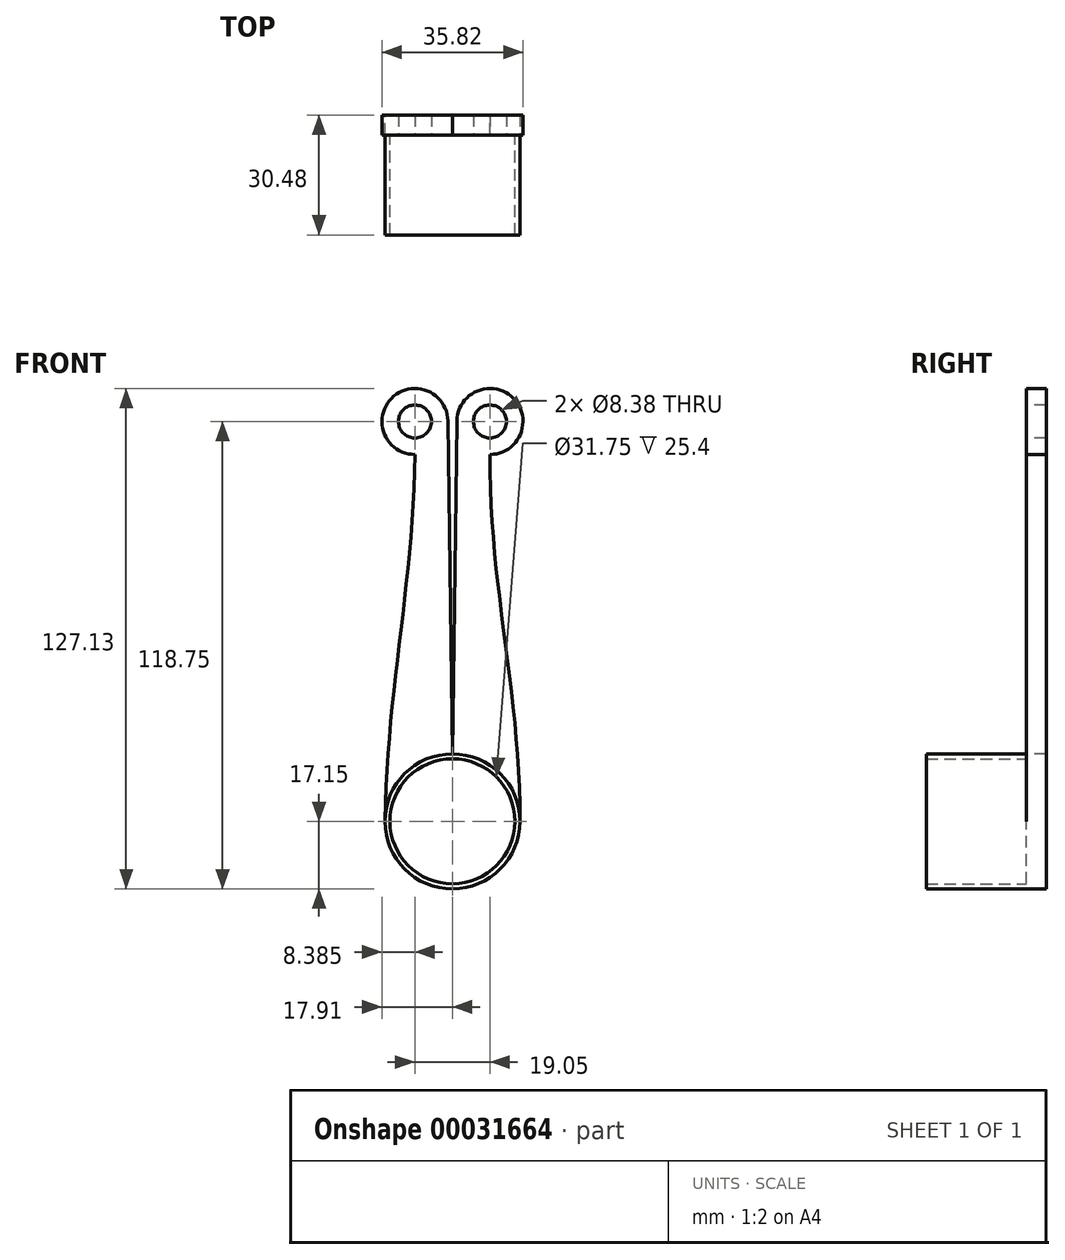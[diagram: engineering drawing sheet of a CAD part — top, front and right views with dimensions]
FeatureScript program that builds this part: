
annotation { "Feature Type Name" : "Feature", "Feature Type Description" : "" }
export const myFeature = defineFeature(function(context is Context, id is Id, definition is map)
    precondition{}
    {
        {
            var Q0;
            Q0=qCreatedBy(makeId("Front.planeOp"),FACE);
            var sketch = newSketch(context, id + "F0", { "sketchPlane" : qUnion([Q0])});
            skCircle(sketch, "E0", {"center": v(0, 0) * mm, "radius": 15.88 * mm});
            skCircle(sketch, "E1", {"center": v(0, 0) * mm, "radius": 17.15 * mm});
            skSolve(sketch);
        }
        {
            var Q0;
            Q0=makeQuery(id+"F0.imprint","IMPRINT",FACE,{"disambiguationData":[TD([[makeQuery(id+"F0.imprint","IMPRINT",EDGE,{"derivedFrom":sQuery(id+"F0.wireOp",EDGE,"E0")}),-1.0]])]});
            extrude(context, id + "F1", {"entities" : qUnion([Q0]), "depth" : 25.4 * mm});
        }
        {
            var Q0;
            Q0=makeQuery(id+"F1.opExtrude","CAP_FACE",FACE,{"disambiguationData":[OSD([sQuery(id+"F0.wireOp",EDGE,"E0"),sQuery(id+"F0.wireOp",EDGE,"E1")])],"isStart":true});
            var sketch = newSketch(context, id + "F2", { "sketchPlane" : qUnion([Q0])});
            skCircle(sketch, "E2", {"center": v(0, 0) * mm, "radius": 17.15 * mm});
            skSolve(sketch);
        }
        {
            var Q0;
            Q0 = qSketchRegion(id + "F2", true);
            extrude(context, id + "F3", {"entities" : qUnion([Q0]), "operationType" : NewBodyOperationType.ADD, "depth" : 5.08 * mm});
        }
        {
            var Q0;
            Q0=makeQuery(id+"F3.opExtrude","CAP_FACE",FACE,{"disambiguationData":[OSD([sQuery(id+"F2.wireOp",EDGE,"E2")])],"isStart":true});
            var sketch = newSketch(context, id + "F4", { "sketchPlane" : qUnion([Q0])});
            skCircle(sketch, "E3", {"center": v(9.52, 101.6) * mm, "radius": 4.2 * mm});
            skCircle(sketch, "E4", {"center": v(-9.53, 101.6) * mm, "radius": 4.2 * mm});
            skArc(sketch, "E5", {"start": v(9.52, 93.22) * mm, "mid": v(15.5, 107.49) * mm, "end": v(1.14, 101.71) * mm});
            skArc(sketch, "E6", {"start": v(-1.14, 101.71) * mm, "mid": v(-15.5, 107.49) * mm, "end": v(-9.53, 93.22) * mm});
            skFitSpline(sketch, "E7", {"points": [v(9.53, 93.22) * mm, v(17.15, 0) * mm], "startDerivative": vector(-0.58, -101.33) * mm, "endDerivative": vector(0, -101.33) * mm});
            skFitSpline(sketch, "E8", {"points": [v(-9.53, 93.22) * mm, v(-17.15, 0) * mm], "startDerivative": vector(-1.5, -101.25) * mm, "endDerivative": vector(-1.62, -101.25) * mm});
            skLineSegment(sketch, "E9", {"start": v(1.14, 101.71) * mm, "end": v(0, 17.14) * mm});
            skLineSegment(sketch, "E10", {"start": v(0, 17.14) * mm, "end": v(-1.14, 101.71) * mm});
            skArc(sketch, "E11", {"start": v(17.15, 0) * mm, "mid": v(0.15, 17.14) * mm, "end": v(-17.14, 0.3) * mm});
            skSolve(sketch);
        }
        {
            var Q0;
            Q0 = qSketchRegion(id + "F4", true);
            var Q1;
            Q1=makeQuery(id+"F3.opExtrude","CAP_FACE",FACE,{"disambiguationData":[OSD([sQuery(id+"F2.wireOp",EDGE,"E2")])],"isStart":false});
            extrude(context, id + "F5", {"entities" : qUnion([Q0]), "operationType" : NewBodyOperationType.ADD, "endBound" : BoundingType.UP_TO_SURFACE, "oppositeDirection" : true, "endBoundEntityFace" : qUnion([Q1]), "depth" : 25.4 * mm});
        }
    });
